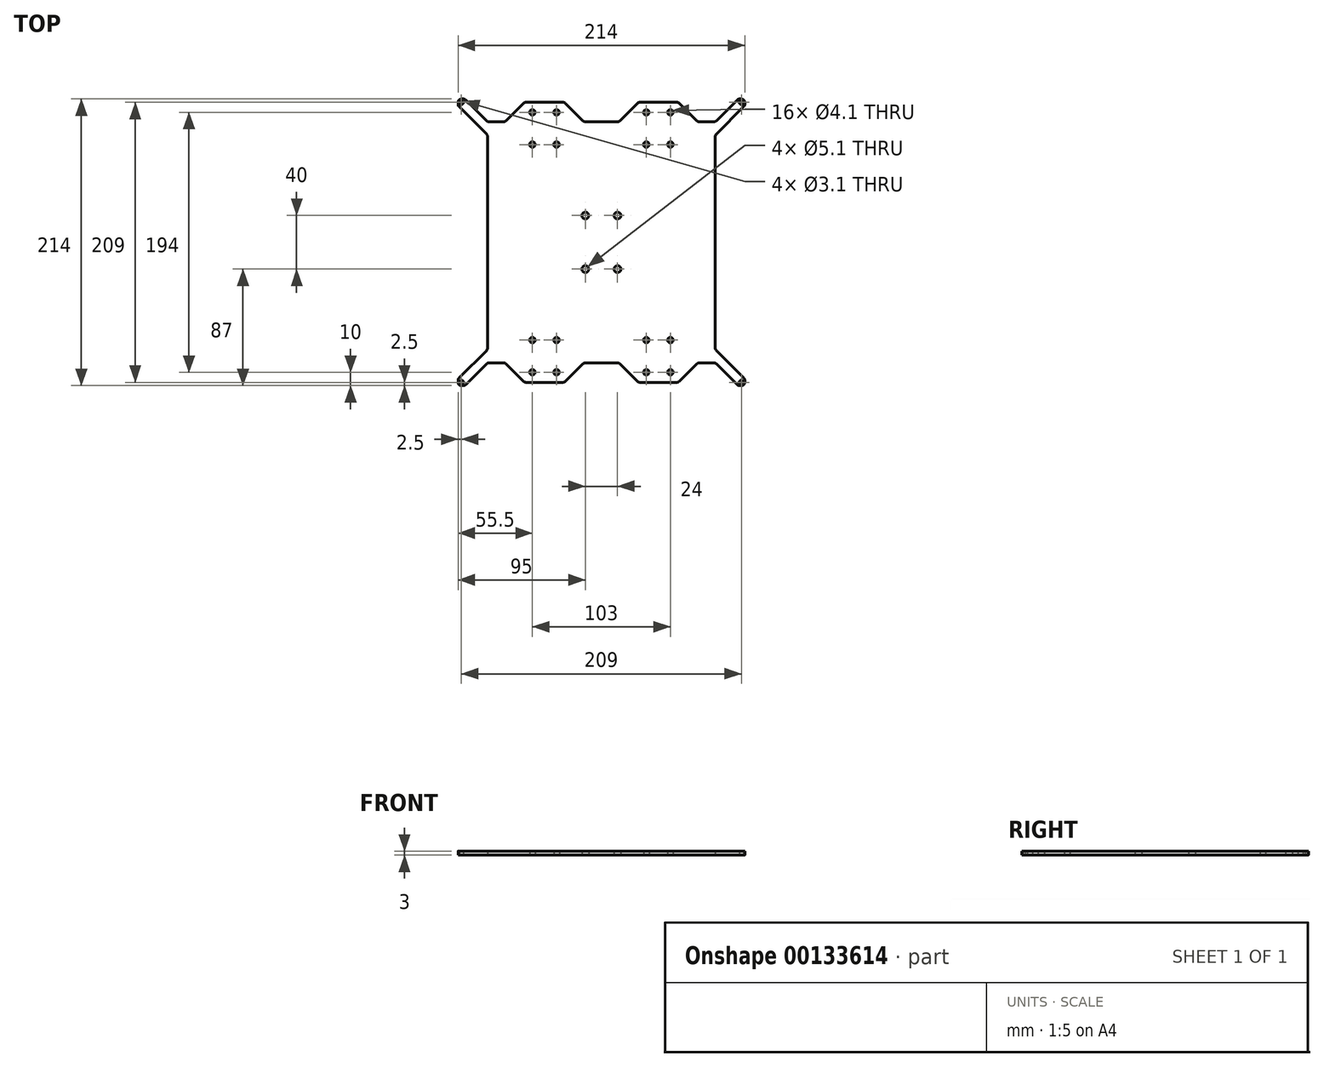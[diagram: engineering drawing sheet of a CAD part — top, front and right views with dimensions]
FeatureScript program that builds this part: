
annotation { "Feature Type Name" : "Feature", "Feature Type Description" : "" }
export const myFeature = defineFeature(function(context is Context, id is Id, definition is map)
    precondition{}
    {
        {
            var Q0;
            Q0=qCreatedBy(makeId("Top.planeOp"),FACE);
            var sketch = newSketch(context, id + "F0", { "sketchPlane" : qUnion([Q0])});
            skLineSegment(sketch, "E0.bottom", {"start": v(104.5, -104.5) * mm, "end": v(-104.5, -104.5) * mm, "construction": true});
            skLineSegment(sketch, "E0.top", {"start": v(104.5, 104.5) * mm, "end": v(-104.5, 104.5) * mm, "construction": true});
            skLineSegment(sketch, "E0.left", {"start": v(104.5, -104.5) * mm, "end": v(104.5, 104.5) * mm, "construction": true});
            skLineSegment(sketch, "E0.right", {"start": v(-104.5, -104.5) * mm, "end": v(-104.5, 104.5) * mm, "construction": true});
            skPoint(sketch, "E0.middle", {"position": v(0, 0) * mm});
            skCircle(sketch, "E1", {"center": v(-104.5, -104.5) * mm, "radius": 1.55 * mm});
            skCircle(sketch, "E2", {"center": v(104.5, -104.5) * mm, "radius": 1.55 * mm});
            skCircle(sketch, "E3", {"center": v(104.5, 104.5) * mm, "radius": 1.55 * mm});
            skCircle(sketch, "E4", {"center": v(-104.5, 104.5) * mm, "radius": 1.55 * mm});
            skLineSegment(sketch, "E5.bottom", {"start": v(85, -85) * mm, "end": v(-85, -85) * mm, "construction": true});
            skLineSegment(sketch, "E5.top", {"start": v(85, 85) * mm, "end": v(-85, 85) * mm, "construction": true});
            skLineSegment(sketch, "E5.left", {"start": v(85, -85) * mm, "end": v(85, 85) * mm, "construction": true});
            skLineSegment(sketch, "E5.right", {"start": v(-85, -85) * mm, "end": v(-85, 85) * mm, "construction": true});
            skLineSegment(sketch, "E6", {"start": v(-85, 0) * mm, "end": v(0, 0) * mm, "construction": true});
            skLineSegment(sketch, "E7", {"start": v(85, 0) * mm, "end": v(0, 0) * mm, "construction": true});
            skLineSegment(sketch, "E8", {"start": v(-42.5, 0) * mm, "end": v(-42.5, 85) * mm, "construction": true});
            skLineSegment(sketch, "E9", {"start": v(42.5, 0) * mm, "end": v(42.5, 85) * mm, "construction": true});
            skLineSegment(sketch, "E10", {"start": v(-42.5, 0) * mm, "end": v(-42.5, -85) * mm, "construction": true});
            skLineSegment(sketch, "E11", {"start": v(42.5, 0) * mm, "end": v(42.5, -85) * mm, "construction": true});
            skLineSegment(sketch, "E12.bottom", {"start": v(-33.5, -73) * mm, "end": v(-51.5, -73) * mm, "construction": true});
            skLineSegment(sketch, "E12.top", {"start": v(-33.5, -97) * mm, "end": v(-51.5, -97) * mm, "construction": true});
            skLineSegment(sketch, "E12.left", {"start": v(-33.5, -73) * mm, "end": v(-33.5, -97) * mm, "construction": true});
            skLineSegment(sketch, "E12.right", {"start": v(-51.5, -73) * mm, "end": v(-51.5, -97) * mm, "construction": true});
            skPoint(sketch, "E12.middle", {"position": v(-42.5, -85) * mm});
            skLineSegment(sketch, "E13.bottom", {"start": v(51.5, -73) * mm, "end": v(33.5, -73) * mm, "construction": true});
            skLineSegment(sketch, "E13.top", {"start": v(51.5, -97) * mm, "end": v(33.5, -97) * mm, "construction": true});
            skLineSegment(sketch, "E13.left", {"start": v(51.5, -73) * mm, "end": v(51.5, -97) * mm, "construction": true});
            skLineSegment(sketch, "E13.right", {"start": v(33.5, -73) * mm, "end": v(33.5, -97) * mm, "construction": true});
            skPoint(sketch, "E13.middle", {"position": v(42.5, -85) * mm});
            skLineSegment(sketch, "E14.bottom", {"start": v(51.5, 73) * mm, "end": v(33.5, 73) * mm, "construction": true});
            skLineSegment(sketch, "E14.top", {"start": v(51.5, 97) * mm, "end": v(33.5, 97) * mm, "construction": true});
            skLineSegment(sketch, "E14.left", {"start": v(51.5, 73) * mm, "end": v(51.5, 97) * mm, "construction": true});
            skLineSegment(sketch, "E14.right", {"start": v(33.5, 73) * mm, "end": v(33.5, 97) * mm, "construction": true});
            skPoint(sketch, "E14.middle", {"position": v(42.5, 85) * mm});
            skLineSegment(sketch, "E15.bottom", {"start": v(-33.5, 73) * mm, "end": v(-51.5, 73) * mm, "construction": true});
            skLineSegment(sketch, "E15.top", {"start": v(-33.5, 97) * mm, "end": v(-51.5, 97) * mm, "construction": true});
            skLineSegment(sketch, "E15.left", {"start": v(-33.5, 73) * mm, "end": v(-33.5, 97) * mm, "construction": true});
            skLineSegment(sketch, "E15.right", {"start": v(-51.5, 73) * mm, "end": v(-51.5, 97) * mm, "construction": true});
            skPoint(sketch, "E15.middle", {"position": v(-42.5, 85) * mm});
            skCircle(sketch, "E16", {"center": v(-51.5, -73) * mm, "radius": 2.05 * mm});
            skCircle(sketch, "E17", {"center": v(-33.5, -73) * mm, "radius": 2.05 * mm});
            skCircle(sketch, "E18", {"center": v(-51.5, -97) * mm, "radius": 2.05 * mm});
            skCircle(sketch, "E19", {"center": v(-33.5, -97) * mm, "radius": 2.05 * mm});
            skCircle(sketch, "E20", {"center": v(33.5, -73) * mm, "radius": 2.05 * mm});
            skCircle(sketch, "E21", {"center": v(33.5, -97) * mm, "radius": 2.05 * mm});
            skCircle(sketch, "E22", {"center": v(51.5, -73) * mm, "radius": 2.05 * mm});
            skCircle(sketch, "E23", {"center": v(51.5, -97) * mm, "radius": 2.05 * mm});
            skCircle(sketch, "E24", {"center": v(-51.5, 97) * mm, "radius": 2.05 * mm});
            skCircle(sketch, "E25", {"center": v(-51.5, 73) * mm, "radius": 2.05 * mm});
            skCircle(sketch, "E26", {"center": v(-33.5, 73) * mm, "radius": 2.05 * mm});
            skCircle(sketch, "E27", {"center": v(-33.5, 97) * mm, "radius": 2.05 * mm});
            skCircle(sketch, "E28", {"center": v(33.5, 97) * mm, "radius": 2.05 * mm});
            skCircle(sketch, "E29", {"center": v(33.5, 73) * mm, "radius": 2.05 * mm});
            skCircle(sketch, "E30", {"center": v(51.5, 73) * mm, "radius": 2.05 * mm});
            skCircle(sketch, "E31", {"center": v(51.5, 97) * mm, "radius": 2.05 * mm});
            skLineSegment(sketch, "E32.bottom", {"start": v(104.5, -107) * mm, "end": v(-104.5, -107) * mm, "construction": true});
            skLineSegment(sketch, "E32.top", {"start": v(104.5, 107) * mm, "end": v(-104.5, 107) * mm, "construction": true});
            skLineSegment(sketch, "E32.left", {"start": v(107, -104.5) * mm, "end": v(107, 104.5) * mm, "construction": true});
            skLineSegment(sketch, "E32.right", {"start": v(-107, -104.5) * mm, "end": v(-107, 104.5) * mm, "construction": true});
            skPoint(sketch, "E33.visualSharp", {"position": v(-107, 107) * mm});
            skArc(sketch, "E33.filletArc", {"start": v(-104.5, 107) * mm, "mid": v(-106.27, 106.27) * mm, "end": v(-107, 104.5) * mm});
            skPoint(sketch, "E34.visualSharp", {"position": v(107, 107) * mm});
            skArc(sketch, "E34.filletArc", {"start": v(107, 104.5) * mm, "mid": v(106.27, 106.27) * mm, "end": v(104.5, 107) * mm});
            skPoint(sketch, "E35.visualSharp", {"position": v(107, -107) * mm});
            skArc(sketch, "E35.filletArc", {"start": v(104.5, -107) * mm, "mid": v(106.27, -106.27) * mm, "end": v(107, -104.5) * mm});
            skPoint(sketch, "E36.visualSharp", {"position": v(-107, -107) * mm});
            skArc(sketch, "E36.filletArc", {"start": v(-107, -104.5) * mm, "mid": v(-106.27, -106.27) * mm, "end": v(-104.5, -107) * mm});
            skLineSegment(sketch, "E37.bottom", {"start": v(-27.5, 68) * mm, "end": v(-57.5, 68) * mm, "construction": true});
            skLineSegment(sketch, "E37.top", {"start": v(-27.5, 102) * mm, "end": v(-57.5, 102) * mm, "construction": true});
            skLineSegment(sketch, "E37.left", {"start": v(-27.5, 68) * mm, "end": v(-27.5, 102) * mm, "construction": true});
            skLineSegment(sketch, "E37.right", {"start": v(-57.5, 68) * mm, "end": v(-57.5, 102) * mm, "construction": true});
            skLineSegment(sketch, "E38", {"start": v(-101.27, 106.27) * mm, "end": v(-85.73, 90.73) * mm});
            skLineSegment(sketch, "E39", {"start": v(-83.96, 90) * mm, "end": v(-73.04, 90) * mm});
            skLineSegment(sketch, "E40", {"start": v(-71.27, 90.73) * mm, "end": v(-58.23, 103.77) * mm});
            skLineSegment(sketch, "E41.bottom", {"start": v(27.5, 68) * mm, "end": v(57.5, 68) * mm, "construction": true});
            skLineSegment(sketch, "E41.top", {"start": v(27.5, 102) * mm, "end": v(57.5, 102) * mm, "construction": true});
            skLineSegment(sketch, "E41.left", {"start": v(27.5, 68) * mm, "end": v(27.5, 102) * mm, "construction": true});
            skLineSegment(sketch, "E41.right", {"start": v(57.5, 68) * mm, "end": v(57.5, 102) * mm, "construction": true});
            skLineSegment(sketch, "E42", {"start": v(-26.77, 103.77) * mm, "end": v(-13.73, 90.73) * mm});
            skLineSegment(sketch, "E43", {"start": v(-11.96, 90) * mm, "end": v(11.96, 90) * mm});
            skLineSegment(sketch, "E44", {"start": v(13.73, 90.73) * mm, "end": v(26.77, 103.77) * mm});
            skLineSegment(sketch, "E45", {"start": v(58.23, 103.77) * mm, "end": v(71.27, 90.73) * mm});
            skLineSegment(sketch, "E46", {"start": v(73.04, 90) * mm, "end": v(83.96, 90) * mm});
            skLineSegment(sketch, "E47", {"start": v(85.73, 90.73) * mm, "end": v(101.27, 106.27) * mm});
            skLineSegment(sketch, "E48.MirrorCS", {"start": v(58.23, -103.77) * mm, "end": v(71.27, -90.73) * mm});
            skLineSegment(sketch, "E49.MirrorCS", {"start": v(85.73, -90.73) * mm, "end": v(101.27, -106.27) * mm});
            skLineSegment(sketch, "E50.MirrorCS", {"start": v(73.04, -90) * mm, "end": v(83.96, -90) * mm});
            skLineSegment(sketch, "E51.MirrorCS", {"start": v(13.73, -90.73) * mm, "end": v(26.77, -103.77) * mm});
            skLineSegment(sketch, "E52.MirrorCS", {"start": v(-11.96, -90) * mm, "end": v(11.96, -90) * mm});
            skLineSegment(sketch, "E53.MirrorCS", {"start": v(-26.77, -103.77) * mm, "end": v(-13.73, -90.73) * mm});
            skLineSegment(sketch, "E54.MirrorCS", {"start": v(-71.27, -90.73) * mm, "end": v(-58.23, -103.77) * mm});
            skLineSegment(sketch, "E55.MirrorCS", {"start": v(-101.27, -106.27) * mm, "end": v(-85.73, -90.73) * mm});
            skLineSegment(sketch, "E56.MirrorCS", {"start": v(-83.96, -90) * mm, "end": v(-73.04, -90) * mm});
            skLineSegment(sketch, "E57", {"start": v(-106.27, 101.27) * mm, "end": v(-85.73, 80.73) * mm});
            skLineSegment(sketch, "E58", {"start": v(-85, 78.96) * mm, "end": v(-85, -78.96) * mm});
            skLineSegment(sketch, "E59", {"start": v(-85.73, -80.73) * mm, "end": v(-106.27, -101.27) * mm});
            skLineSegment(sketch, "E60.MirrorCS", {"start": v(85.73, -80.73) * mm, "end": v(106.27, -101.27) * mm});
            skLineSegment(sketch, "E61.MirrorCS", {"start": v(106.27, 101.27) * mm, "end": v(85.73, 80.73) * mm});
            skLineSegment(sketch, "E62.MirrorCS", {"start": v(85, 78.96) * mm, "end": v(85, -78.96) * mm});
            skLineSegment(sketch, "E63.bottom", {"start": v(12, -20) * mm, "end": v(-12, -20) * mm, "construction": true});
            skLineSegment(sketch, "E63.top", {"start": v(12, 20) * mm, "end": v(-12, 20) * mm, "construction": true});
            skLineSegment(sketch, "E63.left", {"start": v(12, -20) * mm, "end": v(12, 20) * mm, "construction": true});
            skLineSegment(sketch, "E63.right", {"start": v(-12, -20) * mm, "end": v(-12, 20) * mm, "construction": true});
            skLineSegment(sketch, "E64.bottom", {"start": v(20, -26) * mm, "end": v(-20, -26) * mm, "construction": true});
            skLineSegment(sketch, "E64.top", {"start": v(20, 26) * mm, "end": v(-20, 26) * mm, "construction": true});
            skLineSegment(sketch, "E64.left", {"start": v(20, -26) * mm, "end": v(20, 26) * mm, "construction": true});
            skLineSegment(sketch, "E64.right", {"start": v(-20, -26) * mm, "end": v(-20, 26) * mm, "construction": true});
            skCircle(sketch, "E65", {"center": v(-12, 20) * mm, "radius": 2.55 * mm});
            skCircle(sketch, "E66", {"center": v(12, 20) * mm, "radius": 2.55 * mm});
            skCircle(sketch, "E67", {"center": v(-12, -20) * mm, "radius": 2.55 * mm});
            skCircle(sketch, "E68", {"center": v(12, -20) * mm, "radius": 2.55 * mm});
            skLineSegment(sketch, "E69", {"start": v(-56.46, 104.5) * mm, "end": v(-28.54, 104.5) * mm});
            skLineSegment(sketch, "E70", {"start": v(28.54, 104.5) * mm, "end": v(56.46, 104.5) * mm});
            skLineSegment(sketch, "E71", {"start": v(-56.46, -104.5) * mm, "end": v(-28.54, -104.5) * mm});
            skLineSegment(sketch, "E72", {"start": v(28.54, -104.5) * mm, "end": v(56.46, -104.5) * mm});
            skLineSegment(sketch, "E73.bottom", {"start": v(-27.5, -102) * mm, "end": v(-57.5, -102) * mm, "construction": true});
            skLineSegment(sketch, "E73.top", {"start": v(-27.5, -68) * mm, "end": v(-57.5, -68) * mm, "construction": true});
            skLineSegment(sketch, "E73.left", {"start": v(-27.5, -102) * mm, "end": v(-27.5, -68) * mm, "construction": true});
            skLineSegment(sketch, "E73.right", {"start": v(-57.5, -102) * mm, "end": v(-57.5, -68) * mm, "construction": true});
            skLineSegment(sketch, "E74.bottom", {"start": v(27.5, -102) * mm, "end": v(57.5, -102) * mm, "construction": true});
            skLineSegment(sketch, "E74.top", {"start": v(27.5, -68) * mm, "end": v(57.5, -68) * mm, "construction": true});
            skLineSegment(sketch, "E74.left", {"start": v(27.5, -102) * mm, "end": v(27.5, -68) * mm, "construction": true});
            skLineSegment(sketch, "E74.right", {"start": v(57.5, -102) * mm, "end": v(57.5, -68) * mm, "construction": true});
            skLineSegment(sketch, "E75", {"start": v(103.04, 107) * mm, "end": v(104.5, 107) * mm});
            skLineSegment(sketch, "E76", {"start": v(107, 103.04) * mm, "end": v(107, 104.5) * mm});
            skLineSegment(sketch, "E77", {"start": v(107, -104.5) * mm, "end": v(107, -103.04) * mm});
            skLineSegment(sketch, "E78", {"start": v(103.04, -107) * mm, "end": v(104.5, -107) * mm});
            skLineSegment(sketch, "E79", {"start": v(-104.5, -107) * mm, "end": v(-103.04, -107) * mm});
            skLineSegment(sketch, "E80", {"start": v(-107, -104.5) * mm, "end": v(-107, -103.04) * mm});
            skLineSegment(sketch, "E81", {"start": v(-107, 104.5) * mm, "end": v(-107, 103.04) * mm});
            skLineSegment(sketch, "E82", {"start": v(-104.5, 107) * mm, "end": v(-103.04, 107) * mm});
            skPoint(sketch, "E83.visualSharp", {"position": v(-107, 102) * mm});
            skArc(sketch, "E83.filletArc", {"start": v(-107, 103.04) * mm, "mid": v(-106.8, 102.08) * mm, "end": v(-106.27, 101.27) * mm});
            skPoint(sketch, "E84.visualSharp", {"position": v(-102, 107) * mm});
            skArc(sketch, "E84.filletArc", {"start": v(-101.27, 106.27) * mm, "mid": v(-102.08, 106.8) * mm, "end": v(-103.04, 107) * mm});
            skPoint(sketch, "E85.visualSharp", {"position": v(-85, 90) * mm});
            skArc(sketch, "E85.filletArc", {"start": v(-85.73, 90.73) * mm, "mid": v(-84.92, 90.2) * mm, "end": v(-83.96, 90) * mm});
            skPoint(sketch, "E86.visualSharp", {"position": v(-72, 90) * mm});
            skArc(sketch, "E86.filletArc", {"start": v(-73.04, 90) * mm, "mid": v(-72.08, 90.2) * mm, "end": v(-71.27, 90.73) * mm});
            skPoint(sketch, "E87.visualSharp", {"position": v(-57.5, 104.5) * mm});
            skArc(sketch, "E87.filletArc", {"start": v(-56.46, 104.5) * mm, "mid": v(-57.42, 104.3) * mm, "end": v(-58.23, 103.77) * mm});
            skPoint(sketch, "E88.visualSharp", {"position": v(-27.5, 104.5) * mm});
            skArc(sketch, "E88.filletArc", {"start": v(-26.77, 103.77) * mm, "mid": v(-27.58, 104.3) * mm, "end": v(-28.54, 104.5) * mm});
            skPoint(sketch, "E89.visualSharp", {"position": v(-13, 90) * mm});
            skArc(sketch, "E89.filletArc", {"start": v(-13.73, 90.73) * mm, "mid": v(-12.92, 90.2) * mm, "end": v(-11.96, 90) * mm});
            skPoint(sketch, "E90.visualSharp", {"position": v(13, 90) * mm});
            skArc(sketch, "E90.filletArc", {"start": v(11.96, 90) * mm, "mid": v(12.92, 90.2) * mm, "end": v(13.73, 90.73) * mm});
            skPoint(sketch, "E91.visualSharp", {"position": v(27.5, 104.5) * mm});
            skArc(sketch, "E91.filletArc", {"start": v(28.54, 104.5) * mm, "mid": v(27.58, 104.3) * mm, "end": v(26.77, 103.77) * mm});
            skPoint(sketch, "E92.visualSharp", {"position": v(57.5, 104.5) * mm});
            skArc(sketch, "E92.filletArc", {"start": v(58.23, 103.77) * mm, "mid": v(57.42, 104.3) * mm, "end": v(56.46, 104.5) * mm});
            skPoint(sketch, "E93.visualSharp", {"position": v(72, 90) * mm});
            skArc(sketch, "E93.filletArc", {"start": v(71.27, 90.73) * mm, "mid": v(72.08, 90.2) * mm, "end": v(73.04, 90) * mm});
            skPoint(sketch, "E94.visualSharp", {"position": v(85, 90) * mm});
            skArc(sketch, "E94.filletArc", {"start": v(83.96, 90) * mm, "mid": v(84.92, 90.2) * mm, "end": v(85.73, 90.73) * mm});
            skPoint(sketch, "E95.visualSharp", {"position": v(102, 107) * mm});
            skArc(sketch, "E95.filletArc", {"start": v(103.04, 107) * mm, "mid": v(102.08, 106.8) * mm, "end": v(101.27, 106.27) * mm});
            skPoint(sketch, "E96.visualSharp", {"position": v(107, 102) * mm});
            skArc(sketch, "E96.filletArc", {"start": v(106.27, 101.27) * mm, "mid": v(106.8, 102.08) * mm, "end": v(107, 103.04) * mm});
            skPoint(sketch, "E97.visualSharp", {"position": v(85, 80) * mm});
            skArc(sketch, "E97.filletArc", {"start": v(85.73, 80.73) * mm, "mid": v(85.2, 79.92) * mm, "end": v(85, 78.96) * mm});
            skPoint(sketch, "E98.visualSharp", {"position": v(85, -80) * mm});
            skArc(sketch, "E98.filletArc", {"start": v(85, -78.96) * mm, "mid": v(85.2, -79.92) * mm, "end": v(85.73, -80.73) * mm});
            skPoint(sketch, "E99.visualSharp", {"position": v(107, -102) * mm});
            skArc(sketch, "E99.filletArc", {"start": v(107, -103.04) * mm, "mid": v(106.8, -102.08) * mm, "end": v(106.27, -101.27) * mm});
            skPoint(sketch, "E100.visualSharp", {"position": v(102, -107) * mm});
            skArc(sketch, "E100.filletArc", {"start": v(101.27, -106.27) * mm, "mid": v(102.08, -106.8) * mm, "end": v(103.04, -107) * mm});
            skPoint(sketch, "E101.visualSharp", {"position": v(85, -90) * mm});
            skArc(sketch, "E101.filletArc", {"start": v(85.73, -90.73) * mm, "mid": v(84.92, -90.2) * mm, "end": v(83.96, -90) * mm});
            skPoint(sketch, "E102.visualSharp", {"position": v(72, -90) * mm});
            skArc(sketch, "E102.filletArc", {"start": v(73.04, -90) * mm, "mid": v(72.08, -90.2) * mm, "end": v(71.27, -90.73) * mm});
            skPoint(sketch, "E103.visualSharp", {"position": v(57.5, -104.5) * mm});
            skArc(sketch, "E103.filletArc", {"start": v(56.46, -104.5) * mm, "mid": v(57.42, -104.3) * mm, "end": v(58.23, -103.77) * mm});
            skPoint(sketch, "E104.visualSharp", {"position": v(27.5, -104.5) * mm});
            skArc(sketch, "E104.filletArc", {"start": v(26.77, -103.77) * mm, "mid": v(27.58, -104.3) * mm, "end": v(28.54, -104.5) * mm});
            skPoint(sketch, "E105.visualSharp", {"position": v(13, -90) * mm});
            skArc(sketch, "E105.filletArc", {"start": v(13.73, -90.73) * mm, "mid": v(12.92, -90.2) * mm, "end": v(11.96, -90) * mm});
            skPoint(sketch, "E106.visualSharp", {"position": v(-13, -90) * mm});
            skArc(sketch, "E106.filletArc", {"start": v(-11.96, -90) * mm, "mid": v(-12.92, -90.2) * mm, "end": v(-13.73, -90.73) * mm});
            skPoint(sketch, "E107.visualSharp", {"position": v(-27.5, -104.5) * mm});
            skArc(sketch, "E107.filletArc", {"start": v(-28.54, -104.5) * mm, "mid": v(-27.58, -104.3) * mm, "end": v(-26.77, -103.77) * mm});
            skPoint(sketch, "E108.visualSharp", {"position": v(-57.5, -104.5) * mm});
            skArc(sketch, "E108.filletArc", {"start": v(-58.23, -103.77) * mm, "mid": v(-57.42, -104.3) * mm, "end": v(-56.46, -104.5) * mm});
            skPoint(sketch, "E109.visualSharp", {"position": v(-72, -90) * mm});
            skArc(sketch, "E109.filletArc", {"start": v(-71.27, -90.73) * mm, "mid": v(-72.08, -90.2) * mm, "end": v(-73.04, -90) * mm});
            skPoint(sketch, "E110.visualSharp", {"position": v(-85, -90) * mm});
            skArc(sketch, "E110.filletArc", {"start": v(-83.96, -90) * mm, "mid": v(-84.92, -90.2) * mm, "end": v(-85.73, -90.73) * mm});
            skPoint(sketch, "E111.visualSharp", {"position": v(-102, -107) * mm});
            skArc(sketch, "E111.filletArc", {"start": v(-103.04, -107) * mm, "mid": v(-102.08, -106.8) * mm, "end": v(-101.27, -106.27) * mm});
            skPoint(sketch, "E112.visualSharp", {"position": v(-107, -102) * mm});
            skArc(sketch, "E112.filletArc", {"start": v(-106.27, -101.27) * mm, "mid": v(-106.8, -102.08) * mm, "end": v(-107, -103.04) * mm});
            skPoint(sketch, "E113.visualSharp", {"position": v(-85, -80) * mm});
            skArc(sketch, "E113.filletArc", {"start": v(-85.73, -80.73) * mm, "mid": v(-85.2, -79.92) * mm, "end": v(-85, -78.96) * mm});
            skPoint(sketch, "E114.visualSharp", {"position": v(-85, 80) * mm});
            skArc(sketch, "E114.filletArc", {"start": v(-85, 78.96) * mm, "mid": v(-85.2, 79.92) * mm, "end": v(-85.73, 80.73) * mm});
            skSolve(sketch);
        }
        {
            var Q0;
            Q0=makeQuery(id+"F0.imprint","IMPRINT",FACE,{"disambiguationData":[TD([[makeQuery(id+"F0.imprint","IMPRINT",EDGE,{"derivedFrom":sQuery(id+"F0.wireOp",EDGE,"E1")}),-1.0]])]});
            extrude(context, id + "F1", {"entities" : qUnion([Q0]), "depth" : 3 * mm});
        }
    });
